FCSTD DOCUMENT  (FreeCAD 0.18R4 (GitTag))
Label: ques test 2
License: All rights reserved
LicenseURL: http://en.wikipedia.org/wiki/All_rights_reserved
objects: Sketcher::SketchObject×1
note: 1 computed .brp shape members not serialized (recipe doc carries the construction recipe); baked Part::Feature solids carry a one-line shape summary decoded from their .brp

FEATURE [Sketcher::SketchObject] Sketch
  sketch-geometry (25):
    g0: Circle CenterX=1e-16 CenterY=0 CenterZ=0 NormalX=0 NormalY=0 NormalZ=1 AngleXU=0 Radius=10
    g1: ArcOfCircle CenterX=1e-16 CenterY=0 CenterZ=0 NormalX=0 NormalY=0 NormalZ=1 AngleXU=0 Radius=20 StartAngle=0 EndAngle=3.14159
    g2: LineSegment StartX=-20 StartY=2.5e-15 StartZ=0 EndX=-20 EndY=-20 EndZ=0
    g3: LineSegment StartX=20 StartY=0 StartZ=0 EndX=20 EndY=-20 EndZ=0
    g4: Circle CenterX=0 CenterY=60 CenterZ=0 NormalX=0 NormalY=0 NormalZ=1 AngleXU=0 Radius=5
    g5: Circle CenterX=0 CenterY=60 CenterZ=0 NormalX=0 NormalY=0 NormalZ=1 AngleXU=0 Radius=12.5
    g6: ArcOfCircle CenterX=0 CenterY=60 CenterZ=0 NormalX=0 NormalY=0 NormalZ=1 AngleXU=0 Radius=20 StartAngle=0.18132 EndAngle=1.5708
    g7: ArcOfCircle CenterX=1e-16 CenterY=0 CenterZ=0 NormalX=0 NormalY=0 NormalZ=1 AngleXU=0 Radius=50 StartAngle=2.0944 EndAngle=3.14159
    g8: ArcOfCircle CenterX=1e-16 CenterY=0 CenterZ=0 NormalX=0 NormalY=0 NormalZ=1 AngleXU=0 Radius=80 StartAngle=2.0944 EndAngle=3.14159
    g9: ArcOfCircle CenterX=-32.5 CenterY=56.2917 CenterZ=0 NormalX=0 NormalY=0 NormalZ=1 AngleXU=0 Radius=15 StartAngle=5.23599 EndAngle=8.37758
    g10: ArcOfCircle CenterX=-65 CenterY=-1.8e-15 CenterZ=0 NormalX=0 NormalY=0 NormalZ=1 AngleXU=0 Radius=15 StartAngle=3.14159 EndAngle=6.28319
    g11: ArcOfCircle CenterX=-1.3e-15 CenterY=6.1e-15 CenterZ=0 NormalX=0 NormalY=0 NormalZ=1 AngleXU=0 Radius=57 StartAngle=2.0944 EndAngle=3.14159
    g12: ArcOfCircle CenterX=1.46e-14 CenterY=-1.7e-14 CenterZ=0 NormalX=0 NormalY=0 NormalZ=1 AngleXU=0 Radius=73 StartAngle=2.0944 EndAngle=3.14159
    g13: ArcOfCircle CenterX=-65 CenterY=-1.8e-15 CenterZ=0 NormalX=0 NormalY=0 NormalZ=1 AngleXU=0 Radius=8 StartAngle=3.14159 EndAngle=6.28319
    g14: ArcOfCircle CenterX=-32.5 CenterY=56.2917 CenterZ=0 NormalX=0 NormalY=0 NormalZ=1 AngleXU=0 Radius=8 StartAngle=5.23599 EndAngle=8.37758
    g15: LineSegment [constr] StartX=1e-16 StartY=0 StartZ=0 EndX=-40 EndY=69.282 EndZ=0
    g16: ArcOfCircle CenterX=-1.83603e-06 CenterY=6.85215e-06 CenterZ=0 NormalX=0 NormalY=0 NormalZ=1 AngleXU=0 Radius=80 StartAngle=1.5708 EndAngle=2.0944
    g17: LineSegment StartX=35 StartY=-20 StartZ=0 EndX=-135 EndY=-20 EndZ=0
    g18: LineSegment StartX=35 StartY=-35 StartZ=0 EndX=-135 EndY=-35 EndZ=0
    g19: LineSegment StartX=35 StartY=-20 StartZ=0 EndX=35 EndY=-35 EndZ=0
    g20: LineSegment StartX=-135 StartY=-20 StartZ=0 EndX=-135 EndY=-35 EndZ=0
    g21: LineSegment StartX=-135 StartY=-20 StartZ=0 EndX=-79.1315 EndY=-5.03007 EndZ=0
    g22: LineSegment StartX=19.6721 StartY=63.6066 StartZ=0 EndX=35 EndY=-20 EndZ=0
    g23: LineSegment StartX=-3 StartY=47.8653 StartZ=0 EndX=-3 EndY=19.7737 EndZ=0
    g24: LineSegment StartX=3 StartY=47.8653 StartZ=0 EndX=3 EndY=19.7737 EndZ=0
  constraints (70):
    c: Diameter(g0) = 20
    c: Diameter(g1) = 40
    c: Coincident(g1,g0)
    c: Coincident(g0,g-1)
    c: PointOnObject(g1,g-1)
    c: PointOnObject(g1,g-1)
    c: Distance(g2) = 20
    c: Coincident(g2,g1)
    c: Vertical(g2)
    c: Equal(g3,g2)
    c: Coincident(g3,g1)
    c: Vertical(g3)
    c: Distance(g4,g0) = 60
    c: Coincident(g5,g4)
    c: Diameter(g5) = 25
    c: Diameter(g4) = 10
    c: PointOnObject(g4,g-2)
    c: Diameter(g6) = 40
    c: Coincident(g6,g4)
    c: Diameter(g7) = 100
    c: Coincident(g7,g0)
    c: PointOnObject(g7,g-1)
    c: Diameter(g9) = 30
    c: Coincident(g8,g0)
    c: PointOnObject(g11,g-1)
    c: PointOnObject(g12,g-1)
    c: Diameter(g13) = 16
    c: Diameter(g14) = 16
    c: Tangent(g14,g12) = -1.5708
    c: Coincident(g10,g13)
    c: Coincident(g14,g9)
    c: Tangent(g9,g7) = 1.5708
    c: Tangent(g10,g7) = 1.5708
    c: Tangent(g13,g11) = 1.5708
    c: Tangent(g12,g13) = -1.5708
    c: Tangent(g10,g8) = -1.5708
    c: Tangent(g9,g8) = -1.5708
    c: Tangent(g14,g11) = 1.5708
    c: PointOnObject(g7,g15)
    c: Angle(g-1,g15) = 2.0944
    c: Coincident(g0,g15)
    c: Tangent(g16,g6) = -1.5708
    c: Horizontal(g17)
    c: Distance(g17) = 170
    c: DistanceX(g-1,g17) = 35
    c: PointOnObject(g3,g17)
    c: Equal(g18,g17)
    c: DistanceY(g18,g17) = 15
    c: DistanceX(g-1,g18) = 35
    c: Angle(g17,g21) = 0.261799
    c: PointOnObject(g21,g10)
    c: PointOnObject(g24,g1)
    c: PointOnObject(g23,g1)
    c: PointOnObject(g24,g5)
    c: PointOnObject(g23,g5)
    c: Vertical(g24)
    c: Vertical(g23)
    c: Distance(g24,g23) = 6
    c: Horizontal(g18)
    c: Coincident(g20,g17)
    c: Coincident(g19,g17)
    c: Coincident(g19,g18)
    c: Coincident(g20,g18)
    c: Coincident(g17,g22)
    c: Tangent(g22,g6) = 1.5708
    c: Coincident(g16,g8)
    c: DistanceY(g4,g6) = 20
    c: Coincident(g21,g17)
    c: DistanceX(g-1,g24) = 3
    c: PointOnObject(g15,g8)
